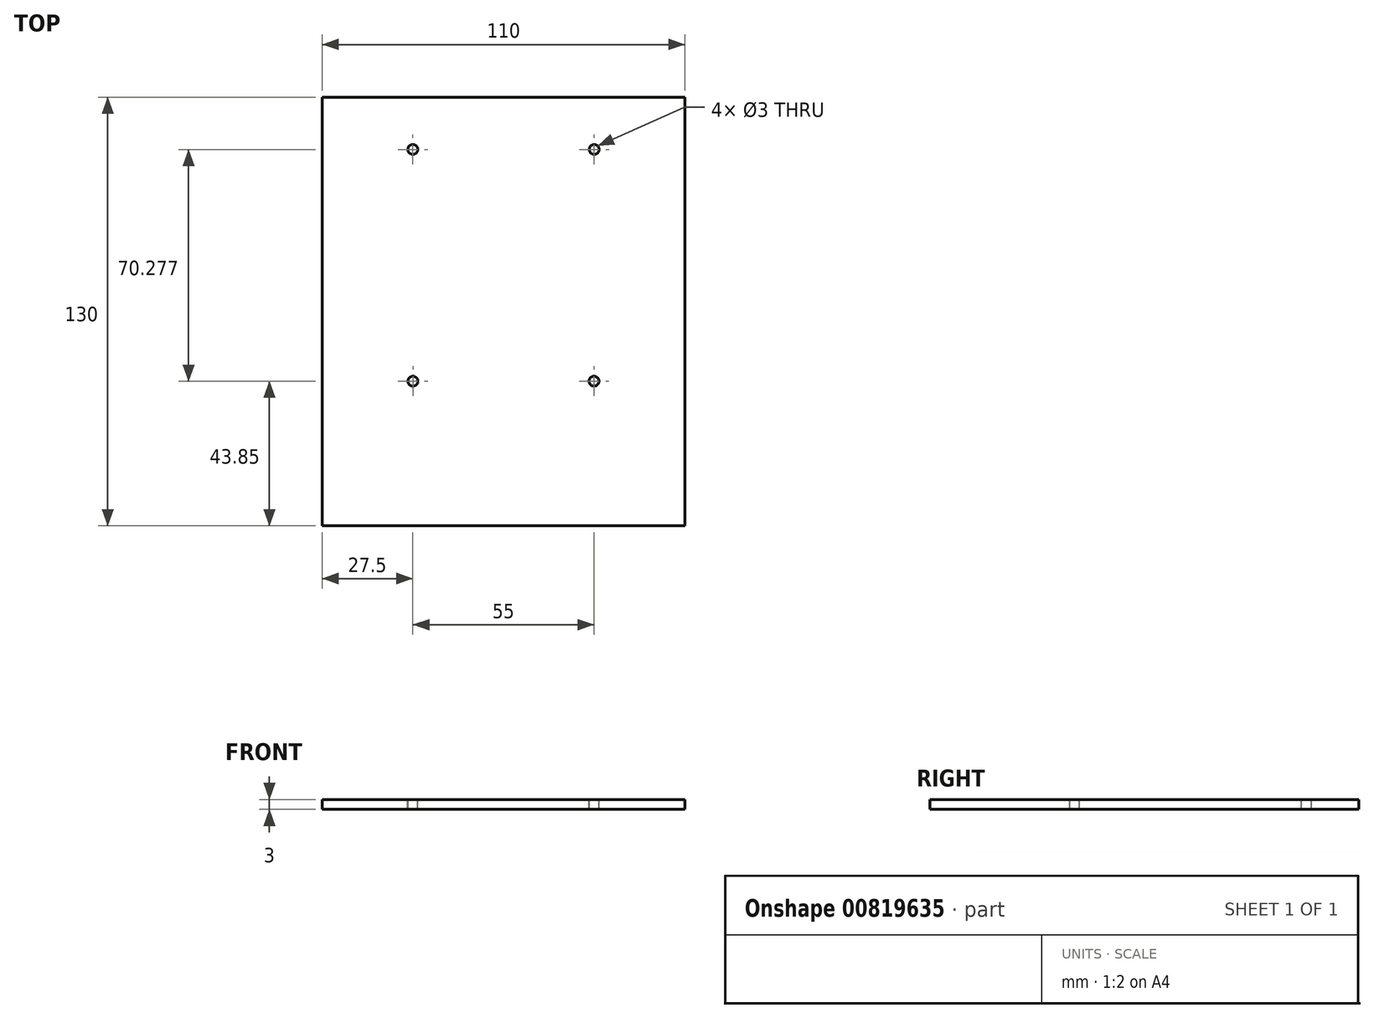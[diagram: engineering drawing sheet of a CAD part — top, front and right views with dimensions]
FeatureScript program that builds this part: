
annotation { "Feature Type Name" : "Feature", "Feature Type Description" : "" }
export const myFeature = defineFeature(function(context is Context, id is Id, definition is map)
    precondition{}
    {
        {
            var Q0;
            Q0=qCreatedBy(makeId("Top.planeOp"),FACE);
            var sketch = newSketch(context, id + "F0", { "sketchPlane" : qUnion([Q0])});
            skLineSegment(sketch, "E0.bottom", {"start": v(0, 0) * mm, "end": v(55, 0) * mm});
            skLineSegment(sketch, "E0.top", {"start": v(0, 130) * mm, "end": v(55, 130) * mm});
            skLineSegment(sketch, "E0.left", {"start": v(0, 0) * mm, "end": v(0, 130) * mm});
            skLineSegment(sketch, "E0.right", {"start": v(55, 0) * mm, "end": v(55, 130) * mm});
            skSolve(sketch);
        }
        {
            var Q0;
            Q0 = qSketchRegion(id + "F0", true);
            var Q1;
            Q1=makeQuery(id+"F0.imprint","IMPRINT",FACE,{"disambiguationData":[TD([[makeQuery(id+"F0.imprint","IMPRINT",EDGE,{"derivedFrom":sQuery(id+"F0.wireOp",EDGE,"E0.bottom")}),1.0]])]});
            extrude(context, id + "F1", {"entities" : qUnion([Q0, Q1]), "depth" : 3 * mm, "offsetDistance" : 25 * mm});
        }
        {
            var Q0;
            Q0=makeQuery(id+"F3yOgWDC90MD5e1_1.imprint","IMPRINT",FACE,{"disambiguationData":[TD([[makeQuery(id+"F3yOgWDC90MD5e1_1.imprint","IMPRINT",EDGE,{"derivedFrom":makeQuery(id+"F1.opExtrude","CAP_EDGE",EDGE,{"disambiguationData":[OSD([sQuery(id+"F0.wireOp",EDGE,"E0.bottom")])],"isStart":false})}),1.0]])]});
            var sketch = newSketch(context, id + "F2", { "sketchPlane" : qUnion([Q0])});
            skLineSegment(sketch, "E1.JIB.JIB", {"start": v(30.83, 49.23) * mm, "end": v(30.83, 84.23) * mm, "construction": true});
            skArc(sketch, "E1.0.startCap", {"start": v(33.33, 49.23) * mm, "mid": v(30.83, 46.73) * mm, "end": v(28.33, 49.23) * mm});
            skArc(sketch, "E1.0.endCap", {"start": v(28.33, 84.23) * mm, "mid": v(30.83, 86.73) * mm, "end": v(33.33, 84.23) * mm});
            skLineSegment(sketch, "E1.0.left", {"start": v(28.33, 49.23) * mm, "end": v(28.33, 84.23) * mm});
            skLineSegment(sketch, "E1.0.right", {"start": v(33.33, 49.23) * mm, "end": v(33.33, 84.23) * mm});
            skSolve(sketch);
        }
        {
            var Q0;
            Q0=makeQuery(id+"F1.opExtrude","CAP_FACE",FACE,{"disambiguationData":[OSD([sQuery(id+"F0.wireOp",EDGE,"E0.bottom"),sQuery(id+"F0.wireOp",EDGE,"E0.top"),sQuery(id+"F0.wireOp",EDGE,"E0.left"),sQuery(id+"F0.wireOp",EDGE,"E0.right")])],"isStart":false});
            var sketch = newSketch(context, id + "F3", { "sketchPlane" : qUnion([Q0])});
            skCircle(sketch, "E2", {"center": v(27.45, 43.85) * mm, "radius": 1.5 * mm});
            skSolve(sketch);
        }
        {
            var Q0;
            Q0=makeQuery(id+"F3.imprint","IMPRINT",FACE,{"disambiguationData":[TD([[makeQuery(id+"F3.imprint","IMPRINT",EDGE,{"derivedFrom":sQuery(id+"F3.wireOp",EDGE,"E2")}),1.0]])]});
            extrude(context, id + "F4", {"entities" : qUnion([Q0]), "operationType" : NewBodyOperationType.REMOVE, "oppositeDirection" : true, "depth" : 25 * mm, "offsetDistance" : 25 * mm});
        }
        {
            var Q0;
            Q0=makeQuery(id+"F1.opExtrude","CAP_FACE",FACE,{"disambiguationData":[OSD([sQuery(id+"F0.wireOp",EDGE,"E0.bottom"),sQuery(id+"F0.wireOp",EDGE,"E0.top"),sQuery(id+"F0.wireOp",EDGE,"E0.left"),sQuery(id+"F0.wireOp",EDGE,"E0.right")])],"isStart":false});
            var sketch = newSketch(context, id + "F5", { "sketchPlane" : qUnion([Q0])});
            skCircle(sketch, "E3", {"center": v(27.5, 114.13) * mm, "radius": 1.5 * mm});
            skPoint(sketch, "E3.centerSnap0", {"position": v(27.5, 130) * mm});
            skSolve(sketch);
        }
        {
            var Q0;
            Q0 = qSketchRegion(id + "F5", true);
            extrude(context, id + "F6", {"entities" : qUnion([Q0]), "operationType" : NewBodyOperationType.REMOVE, "oppositeDirection" : true, "depth" : 25 * mm, "offsetDistance" : 25 * mm});
        }
        {
            var Q0;
            Q0=makeQuery(id+"F1.opExtrude","CAP_FACE",FACE,{"disambiguationData":[OSD([sQuery(id+"F0.wireOp",EDGE,"E0.bottom"),sQuery(id+"F0.wireOp",EDGE,"E0.top"),sQuery(id+"F0.wireOp",EDGE,"E0.left"),sQuery(id+"F0.wireOp",EDGE,"E0.right")])],"isStart":false});
            var sketch = newSketch(context, id + "F7", { "sketchPlane" : qUnion([Q0])});
            skSolve(sketch);
        }
        {
            var Q0;
            Q0=makeQuery(id+"F1.opExtrude","SWEPT_BODY",BODY,{"disambiguationData":[OSD([sQuery(id+"F0.wireOp",EDGE,"E0.bottom"),sQuery(id+"F0.wireOp",EDGE,"E0.top"),sQuery(id+"F0.wireOp",EDGE,"E0.left"),sQuery(id+"F0.wireOp",EDGE,"E0.right")])]});
            var Q1;
            Q1=qCreatedBy(makeId("Right.planeOp"),FACE);
            mirror(context, id + "F8", {"operationType" : NewBodyOperationType.ADD, "entities" : qUnion([Q0]), "mirrorPlane" : qUnion([Q1])});
        }
    });
